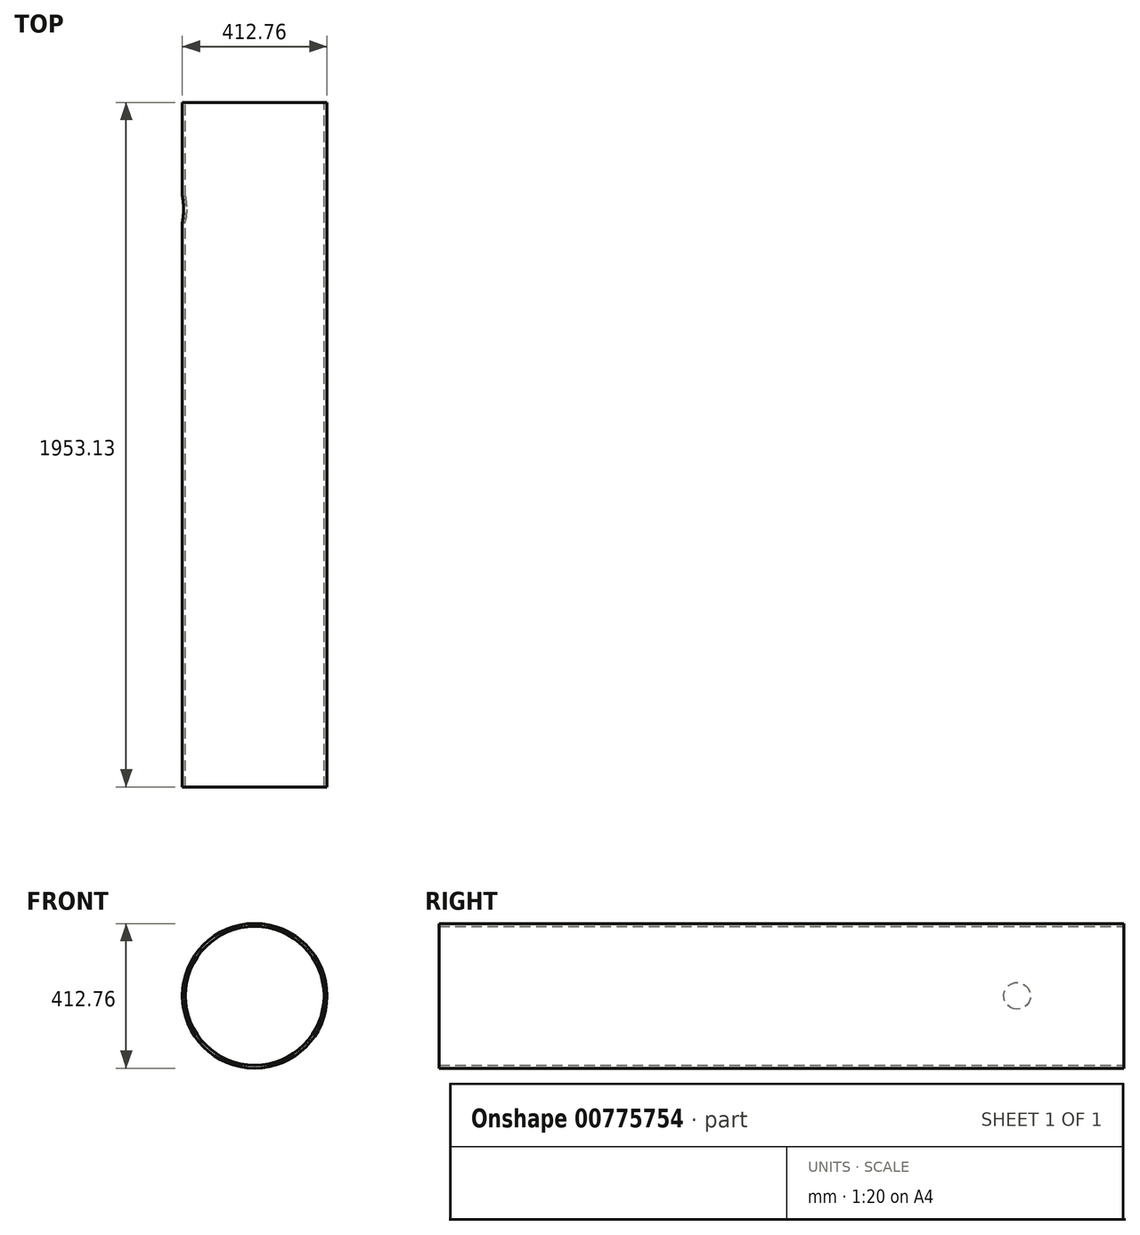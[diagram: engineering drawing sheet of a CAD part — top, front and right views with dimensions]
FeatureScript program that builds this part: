
annotation { "Feature Type Name" : "Feature", "Feature Type Description" : "" }
export const myFeature = defineFeature(function(context is Context, id is Id, definition is map)
    precondition{}
    {
        {
            var Q0;
            Q0=qCreatedBy(makeId("Front.planeOp"),FACE);
            var sketch = newSketch(context, id + "F0", { "sketchPlane" : qUnion([Q0])});
            skCircle(sketch, "E0", {"center": v(0, 0) * mm, "radius": 197.94 * mm});
            skCircle(sketch, "E1", {"center": v(0, 0) * mm, "radius": 206.38 * mm});
            skSolve(sketch);
        }
        {
            var Q0;
            Q0 = qSketchRegion(id + "F0", true);
            extrude(context, id + "F1", {"entities" : qUnion([Q0]), "depth" : 1953.13 * mm, "offsetDistance" : 25.4 * mm});
        }
        {
            var Q0;
            Q0=qCreatedBy(makeId("Right.planeOp"),FACE);
            var sketch = newSketch(context, id + "F2", { "sketchPlane" : qUnion([Q0])});
            skCircle(sketch, "E2", {"center": v(-304.8, 0) * mm, "radius": 38.1 * mm});
            skSolve(sketch);
        }
        {
            var Q0;
            Q0=sQuery(id+"F2.wireOp",VERTEX,"E2.center");
            var Q1;
            Q1=makeQuery(id+"F1.opExtrude","SWEPT_BODY",BODY,{"disambiguationData":[OSD([sQuery(id+"F0.wireOp",EDGE,"E0"),sQuery(id+"F0.wireOp",EDGE,"E1")])]});
            hole(context, id + "F3", {"style" : HoleStyle.SIMPLE, "endStyle" : HoleEndStyle.THROUGH, "holeDiameter" : 76.2 * mm, "majorDiameter" : 6.35 * mm, "isTappedThrough" : true, "tappedDepth" : 12.7 * mm, "tapClearance" : 3, "locations" : qUnion([Q0]), "scope" : qUnion([Q1])});
        }
    });
